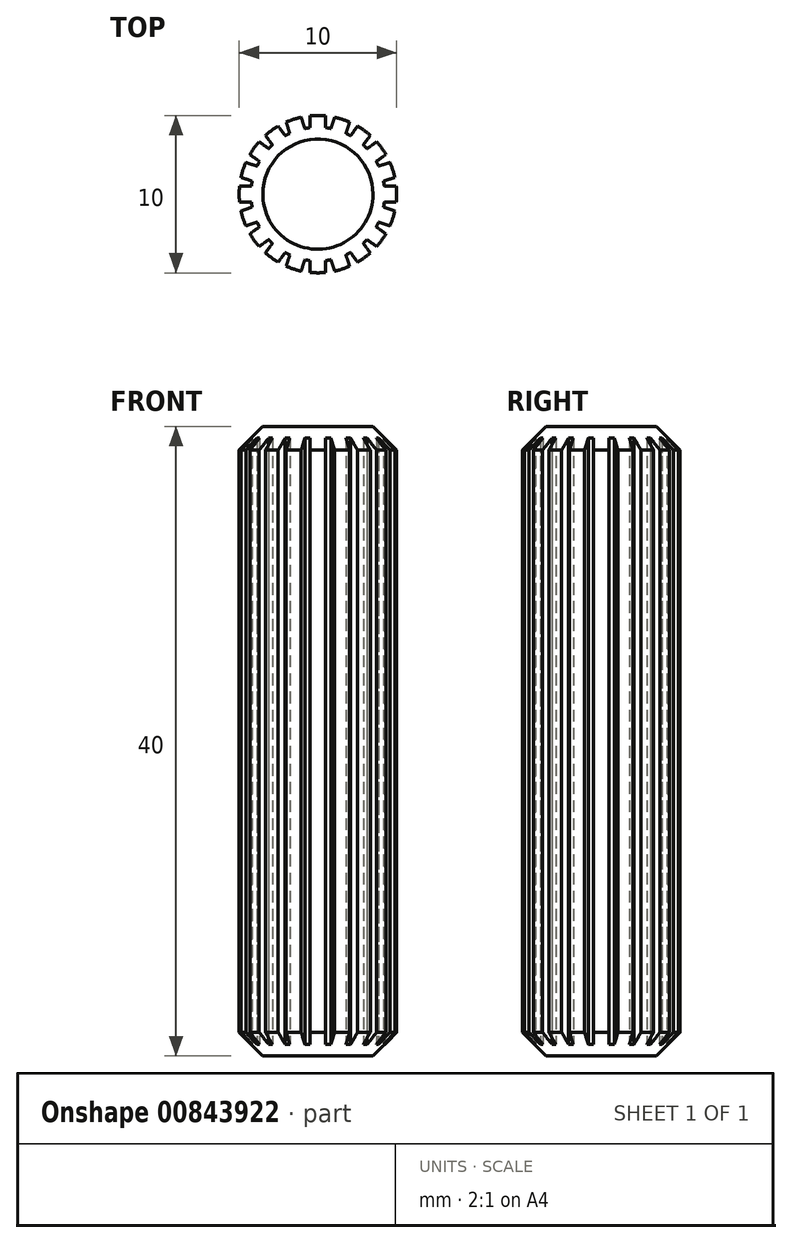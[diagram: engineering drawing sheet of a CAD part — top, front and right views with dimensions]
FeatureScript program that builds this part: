
annotation { "Feature Type Name" : "Feature", "Feature Type Description" : "" }
export const myFeature = defineFeature(function(context is Context, id is Id, definition is map)
    precondition{}
    {
        {
            var Q0;
            Q0=qCreatedBy(makeId("Top.planeOp"),FACE);
            var sketch = newSketch(context, id + "F0", { "sketchPlane" : qUnion([Q0])});
            skCircle(sketch, "E0", {"center": v(0, 0) * mm, "radius": 5 * mm});
            skCircle(sketch, "E1.0", {"center": v(0, 0) * mm, "radius": 4.25 * mm});
            skCircle(sketch, "E2", {"center": v(0, 0) * mm, "radius": 0.5 * mm});
            skLineSegment(sketch, "E3", {"start": v(-0.5, 0) * mm, "end": v(-0.5, 4.97) * mm});
            skLineSegment(sketch, "E4", {"start": v(0.5, 0) * mm, "end": v(0.5, 4.97) * mm});
            skSolve(sketch);
        }
        {
            var Q0;
            {var subQ0=sQuery(id+"F0.wireOp",EDGE,"E3");var subQ1=sQuery(id+"F0.wireOp",EDGE,"E1.0");var subQ2=makeQuery(id+"F0.imprint","INTERSECT",VERTEX,{"derivedFrom":[subQ1,subQ0]});Q0=makeQuery(id+"F0.imprint","IMPRINT",FACE,{"disambiguationData":[TD([[makeQuery(id+"F0.imprint","IMPRINT",EDGE,{"disambiguationData":[TD([[subQ2,-1.0]])],"derivedFrom":subQ1}),1.0]])]});}
            var Q1;
            {var subQ0=sQuery(id+"F0.wireOp",EDGE,"E2");var subQ1=makeQuery(id+"F0.imprint","INTERSECT",VERTEX,{"derivedFrom":[subQ0,sQuery(id+"F0.wireOp",EDGE,"E3")]});Q1=makeQuery(id+"F0.imprint","IMPRINT",FACE,{"disambiguationData":[TD([[makeQuery(id+"F0.imprint","IMPRINT",EDGE,{"disambiguationData":[TD([[subQ1,1.0]])],"derivedFrom":subQ0}),1.0]])]});}
            var Q2;
            {var subQ0=sQuery(id+"F0.wireOp",EDGE,"E3");var subQ1=sQuery(id+"F0.wireOp",EDGE,"E1.0");var subQ2=makeQuery(id+"F0.imprint","INTERSECT",VERTEX,{"derivedFrom":[subQ1,subQ0]});Q2=makeQuery(id+"F0.imprint","IMPRINT",FACE,{"disambiguationData":[TD([[makeQuery(id+"F0.imprint","IMPRINT",EDGE,{"disambiguationData":[TD([[subQ2,1.0]])],"derivedFrom":subQ1}),1.0]])]});}
            extrude(context, id + "F1", {"entities" : qUnion([Q0, Q1, Q2]), "endBound" : BoundingType.SYMMETRIC, "depth" : 40 * mm, "offsetDistance" : 25 * mm});
        }
        {
            var Q0;
            Q0=makeQuery(id+"F1.opExtrude","CAP_EDGE",EDGE,{"disambiguationData":[OSD([sQuery(id+"F0.wireOp",EDGE,"E1.0")])],"isStart":false});
            var Q1;
            Q1=makeQuery(id+"F1.opExtrude","CAP_EDGE",EDGE,{"disambiguationData":[OSD([sQuery(id+"F0.wireOp",EDGE,"E1.0")])],"isStart":true});
            chamfer(context, id + "F2", {"entities" : qUnion([Q0, Q1]), "width" : .75 * mm, "tangentPropagation" : true});
        }
        {
            var Q0;
            {var subQ0=sQuery(id+"F0.wireOp",EDGE,"E3");var subQ1=sQuery(id+"F0.wireOp",EDGE,"E0");var subQ2=makeQuery(id+"F0.imprint","INTERSECT",VERTEX,{"derivedFrom":[subQ1,subQ0]});Q0=makeQuery(id+"F0.imprint","IMPRINT",FACE,{"disambiguationData":[TD([[makeQuery(id+"F0.imprint","IMPRINT",EDGE,{"disambiguationData":[TD([[subQ2,1.0]])],"derivedFrom":subQ1}),1.0]])]});}
            extrude(context, id + "F3", {"entities" : qUnion([Q0]), "operationType" : NewBodyOperationType.ADD, "endBound" : BoundingType.SYMMETRIC, "depth" : 38.5 * mm, "offsetDistance" : 25 * mm});
        }
        {
            var Q0;
            Q0=makeQuery(id+"F3.opExtrude","CAP_EDGE",EDGE,{"disambiguationData":[OSD([sQuery(id+"F0.wireOp",EDGE,"E0")])],"isStart":false});
            var Q1;
            Q1=makeQuery(id+"F3.opExtrude","CAP_EDGE",EDGE,{"disambiguationData":[OSD([sQuery(id+"F0.wireOp",EDGE,"E0")])],"isStart":true});
            chamfer(context, id + "F4", {"entities" : qUnion([Q0, Q1]), "width" : .75 * mm, "tangentPropagation" : true});
        }
        {
            var Q0;
            Q0=makeQuery(id+"F1.opExtrude","SWEPT_BODY",BODY,{"disambiguationData":[OSD([sQuery(id+"F0.wireOp",EDGE,"E1.0")])]});
            var Q1;
            Q1=sQuery(id+"F0.wireOp",EDGE,"E1.0");
            circularPattern(context, id + "F5", {"operationType" : NewBodyOperationType.ADD, "entities" : qUnion([Q0]), "axis" : qUnion([Q1]), "angle" : 360 * degree, "instanceCount" : 20, "equalSpace" : true});
        }
    });
